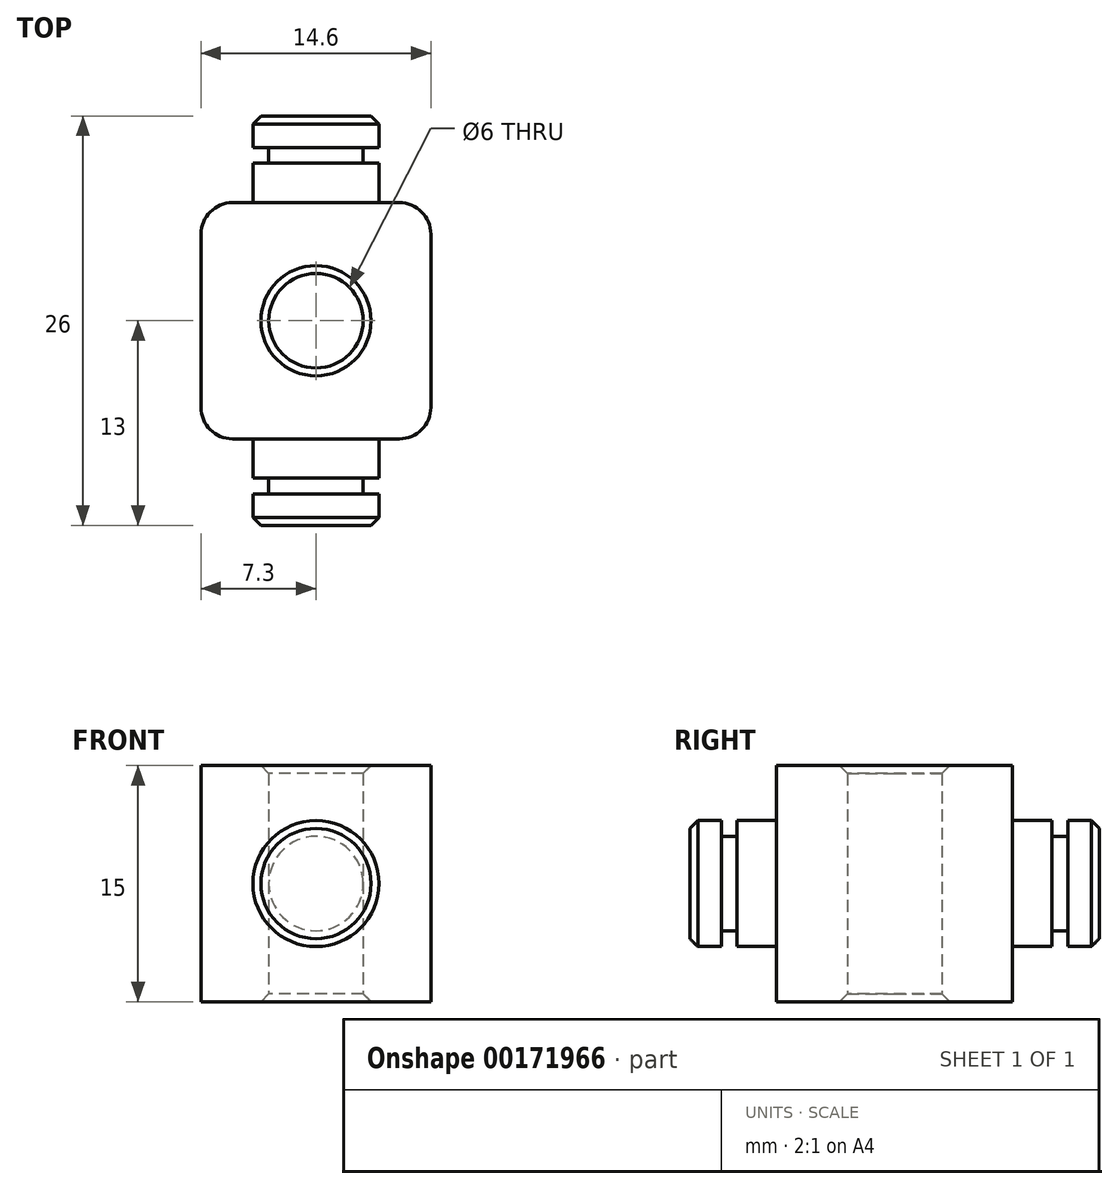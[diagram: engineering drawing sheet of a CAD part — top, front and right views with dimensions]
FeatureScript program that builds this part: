
annotation { "Feature Type Name" : "Feature", "Feature Type Description" : "" }
export const myFeature = defineFeature(function(context is Context, id is Id, definition is map)
    precondition{}
    {
        {
            var Q0;
            Q0=qCreatedBy(makeId("Top.planeOp"),FACE);
            var sketch = newSketch(context, id + "F0", { "sketchPlane" : qUnion([Q0])});
            skLineSegment(sketch, "E0.bottom", {"start": v(5.3, 7.5) * mm, "end": v(-5.3, 7.5) * mm});
            skLineSegment(sketch, "E0.top", {"start": v(5.3, -7.5) * mm, "end": v(-5.3, -7.5) * mm});
            skLineSegment(sketch, "E0.left", {"start": v(7.3, 5.5) * mm, "end": v(7.3, -5.5) * mm});
            skLineSegment(sketch, "E0.right", {"start": v(-7.3, 5.5) * mm, "end": v(-7.3, -5.5) * mm});
            skPoint(sketch, "E0.middle", {"position": v(0, 0) * mm});
            skPoint(sketch, "E1.visualSharp", {"position": v(-7.3, 7.5) * mm});
            skArc(sketch, "E1.filletArc", {"start": v(-5.3, 7.5) * mm, "mid": v(-6.71, 6.91) * mm, "end": v(-7.3, 5.5) * mm});
            skPoint(sketch, "E2.visualSharp", {"position": v(-7.3, -7.5) * mm});
            skArc(sketch, "E2.filletArc", {"start": v(-7.3, -5.5) * mm, "mid": v(-6.71, -6.91) * mm, "end": v(-5.3, -7.5) * mm});
            skPoint(sketch, "E3.visualSharp", {"position": v(7.3, -7.5) * mm});
            skArc(sketch, "E3.filletArc", {"start": v(5.3, -7.5) * mm, "mid": v(6.71, -6.91) * mm, "end": v(7.3, -5.5) * mm});
            skPoint(sketch, "E4.visualSharp", {"position": v(7.3, 7.5) * mm});
            skArc(sketch, "E4.filletArc", {"start": v(7.3, 5.5) * mm, "mid": v(6.71, 6.91) * mm, "end": v(5.3, 7.5) * mm});
            skCircle(sketch, "E5", {"center": v(0, 0) * mm, "radius": 3 * mm});
            skSolve(sketch);
        }
        {
            var Q0;
            Q0=makeQuery(id+"F0.imprint","IMPRINT",FACE,{"disambiguationData":[TD([[makeQuery(id+"F0.imprint","IMPRINT",EDGE,{"derivedFrom":sQuery(id+"F0.wireOp",EDGE,"E0.bottom")}),1.0]])]});
            extrude(context, id + "F1", {"entities" : qUnion([Q0]), "endBound" : BoundingType.SYMMETRIC, "depth" : 15 * mm});
        }
        {
            var Q0;
            Q0=makeQuery(id+"F1.opExtrude","CAP_EDGE",EDGE,{"disambiguationData":[OSD([sQuery(id+"F0.wireOp",EDGE,"E5")])],"isStart":false});
            var Q1;
            Q1=makeQuery(id+"F1.opExtrude","CAP_EDGE",EDGE,{"disambiguationData":[OSD([sQuery(id+"F0.wireOp",EDGE,"E5")])],"isStart":true});
            chamfer(context, id + "F2", {"entities" : qUnion([Q0, Q1]), "chamferType" : ChamferType.OFFSET_ANGLE, "width" : .5 * mm, "oppositeDirection" : false, "angle" : 45 * degree, "tangentPropagation" : true});
        }
        {
            var Q0;
            Q0=makeQuery(id+"F1.opExtrude","SWEPT_FACE",FACE,{"disambiguationData":[OSD([sQuery(id+"F0.wireOp",EDGE,"E0.top")])]});
            var sketch = newSketch(context, id + "F3", { "sketchPlane" : qUnion([Q0])});
            skCircle(sketch, "E6", {"center": v(0, 0) * mm, "radius": 4 * mm});
            skPoint(sketch, "E6.centerSnap0", {"position": v(0, 7.5) * mm});
            skPoint(sketch, "E6.centerSnap1", {"position": v(5.3, 0) * mm});
            skSolve(sketch);
        }
        {
            var Q0;
            Q0=makeQuery(id+"F3.imprint","IMPRINT",FACE,{"disambiguationData":[TD([[makeQuery(id+"F3.imprint","IMPRINT",EDGE,{"derivedFrom":sQuery(id+"F3.wireOp",EDGE,"E6")}),1.0]])]});
            extrude(context, id + "F4", {"entities" : qUnion([Q0]), "operationType" : NewBodyOperationType.ADD, "depth" : 5.5 * mm});
        }
        {
            var Q0;
            Q0=makeQuery(id+"F4.opExtrude","CAP_EDGE",EDGE,{"disambiguationData":[OSD([sQuery(id+"F3.wireOp",EDGE,"E6")])],"isStart":false});
            chamfer(context, id + "F5", {"entities" : qUnion([Q0]), "chamferType" : ChamferType.OFFSET_ANGLE, "width" : .5 * mm, "oppositeDirection" : false, "angle" : 45 * degree, "tangentPropagation" : true});
        }
        {
            var Q0;
            Q0=qCreatedBy(makeId("Right.planeOp"),FACE);
            var sketch = newSketch(context, id + "F6", { "sketchPlane" : qUnion([Q0])});
            skLineSegment(sketch, "E7.bottom", {"start": v(-11, 4) * mm, "end": v(-10, 4) * mm});
            skLineSegment(sketch, "E7.top", {"start": v(-11, 3) * mm, "end": v(-10, 3) * mm});
            skLineSegment(sketch, "E7.left", {"start": v(-11, 4) * mm, "end": v(-11, 3) * mm});
            skLineSegment(sketch, "E7.right", {"start": v(-10, 4) * mm, "end": v(-10, 3) * mm});
            skSolve(sketch);
        }
        {
            var Q0;
            Q0 = qSketchRegion(id + "F6", true);
            var Q1;
            {var subQ0=sQuery(id+"F3.wireOp",EDGE,"E6");Q1=makeQuery(id+"F5.opChamfer","BLEND_EDGE",EDGE,{"blendedFrom":[makeQuery(id+"F4.opExtrude","CAP_EDGE",EDGE,{"disambiguationData":[OSD([subQ0])],"isStart":false}),makeQuery(id+"F4.opExtrude","CAP_FACE",FACE,{"disambiguationData":[OSD([subQ0])],"isStart":false})],"blendedInto":[makeQuery(id+"F4.opExtrude","CAP_FACE",FACE,{"disambiguationData":[OSD([subQ0])],"isStart":false})]});}
            revolve(context, id + "F7", {"operationType" : NewBodyOperationType.REMOVE, "entities" : qUnion([Q0]), "axis" : qUnion([Q1]), "revolveType" : RevolveType.FULL, "oppositeDirection" : true});
        }
        {
            var Q0;
            Q0=makeQuery(id+"F4.opExtrude","CAP_FACE",FACE,{"disambiguationData":[OSD([sQuery(id+"F3.wireOp",EDGE,"E6")])],"isStart":false});
            var Q1;
            Q1=makeQuery(id+"F5.opChamfer","BLEND_FACE",FACE,{"disambiguationData":[OSD([sQuery(id+"F3.wireOp",EDGE,"E6")])]});
            var Q2;
            {var subQ0=sQuery(id+"F3.wireOp",EDGE,"E6");Q2=makeQuery(id+"F7.boolean.opBoolean","SPLIT",FACE,{"disambiguationData":[TD([makeQuery(id+"F5.opChamfer","BLEND_FACE",FACE,{"disambiguationData":[OSD([subQ0])]})])],"derivedFrom":makeQuery(id+"F4.opExtrude","SWEPT_FACE",FACE,{"disambiguationData":[OSD([subQ0])]})});}
            var Q3;
            Q3=makeQuery(id+"F7.boolean.opBoolean","SPLIT",FACE,{"disambiguationData":[TD([makeQuery(id+"F1.opExtrude","SWEPT_FACE",FACE,{"disambiguationData":[OSD([sQuery(id+"F0.wireOp",EDGE,"E0.top")])]})])],"derivedFrom":makeQuery(id+"F4.opExtrude","SWEPT_FACE",FACE,{"disambiguationData":[OSD([sQuery(id+"F3.wireOp",EDGE,"E6")])]})});
            var Q4;
            Q4=makeQuery(id+"F7.boolean.opBoolean","COPY",FACE,{"derivedFrom":makeQuery(id+"F7.opRevolve","SWEPT_FACE",FACE,{"disambiguationData":[OSD([sQuery(id+"F6.wireOp",EDGE,"E7.left")])]})});
            var Q5;
            Q5=makeQuery(id+"F7.boolean.opBoolean","COPY",FACE,{"derivedFrom":makeQuery(id+"F7.opRevolve","SWEPT_FACE",FACE,{"disambiguationData":[OSD([sQuery(id+"F6.wireOp",EDGE,"E7.top")])]})});
            var Q6;
            Q6=makeQuery(id+"F7.boolean.opBoolean","COPY",FACE,{"derivedFrom":makeQuery(id+"F7.opRevolve","SWEPT_FACE",FACE,{"disambiguationData":[OSD([sQuery(id+"F6.wireOp",EDGE,"E7.right")])]})});
            var Q7;
            Q7=qCreatedBy(makeId("Front.planeOp"),FACE);
            mirror(context, id + "F8", {"patternType" : MirrorType.FACE, "faces" : qUnion([Q0, Q1, Q2, Q3, Q4, Q5, Q6]), "mirrorPlane" : qUnion([Q7])});
        }
    });
